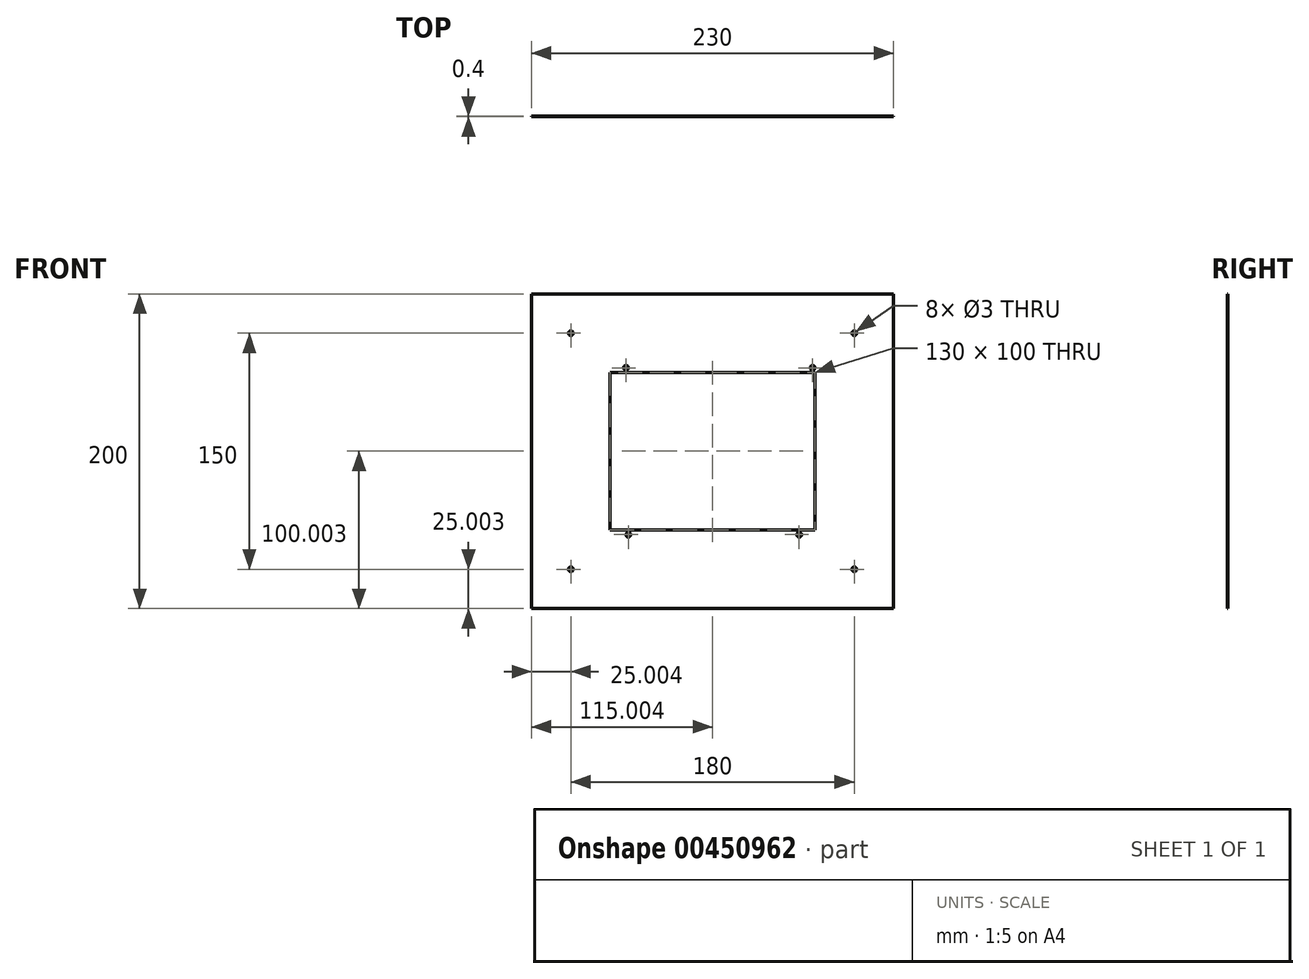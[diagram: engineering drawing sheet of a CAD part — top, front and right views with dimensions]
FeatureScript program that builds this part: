
annotation { "Feature Type Name" : "Feature", "Feature Type Description" : "" }
export const myFeature = defineFeature(function(context is Context, id is Id, definition is map)
    precondition{}
    {
        {
            var Q0;
            Q0=qCreatedBy(makeId("Front.planeOp"),FACE);
            var sketch = newSketch(context, id + "F0", { "sketchPlane" : qUnion([Q0])});
            skLineSegment(sketch, "E0.bottom", {"start": v(-111.43, 122.4) * mm, "end": v(118.57, 122.4) * mm});
            skLineSegment(sketch, "E0.top", {"start": v(-111.43, -77.6) * mm, "end": v(118.57, -77.6) * mm});
            skLineSegment(sketch, "E0.left", {"start": v(-111.43, 122.4) * mm, "end": v(-111.43, -77.6) * mm});
            skLineSegment(sketch, "E0.right", {"start": v(118.57, 122.4) * mm, "end": v(118.57, -77.6) * mm});
            skSolve(sketch);
        }
        {
            var Q0;
            Q0 = qSketchRegion(id + "F0", true);
            extrude(context, id + "F1", {"entities" : qUnion([Q0]), "depth" : 0.4 * mm, "offsetDistance" : 25 * mm});
        }
        {
            var Q0;
            Q0=makeQuery(id+"F1.opExtrude","CAP_FACE",FACE,{"disambiguationData":[OSD([sQuery(id+"F0.wireOp",EDGE,"E0.bottom"),sQuery(id+"F0.wireOp",EDGE,"E0.top"),sQuery(id+"F0.wireOp",EDGE,"E0.left"),sQuery(id+"F0.wireOp",EDGE,"E0.right")])],"isStart":false});
            var sketch = newSketch(context, id + "F2", { "sketchPlane" : qUnion([Q0])});
            skLineSegment(sketch, "E1.bottom", {"start": v(-61.43, -27.6) * mm, "end": v(68.57, -27.6) * mm});
            skLineSegment(sketch, "E1.top", {"start": v(-61.43, 72.4) * mm, "end": v(68.57, 72.4) * mm});
            skLineSegment(sketch, "E1.left", {"start": v(-61.43, -27.6) * mm, "end": v(-61.43, 72.4) * mm});
            skLineSegment(sketch, "E1.right", {"start": v(68.57, -27.6) * mm, "end": v(68.57, 72.4) * mm});
            skCircle(sketch, "E2", {"center": v(-49.93, -30.6) * mm, "radius": 1.5 * mm});
            skCircle(sketch, "E3", {"center": v(58.57, -30.6) * mm, "radius": 1.5 * mm});
            skCircle(sketch, "E4", {"center": v(67.07, 75.4) * mm, "radius": 1.5 * mm});
            skCircle(sketch, "E5", {"center": v(-51.43, 75.4) * mm, "radius": 1.5 * mm});
            skCircle(sketch, "E6", {"center": v(-86.43, -52.6) * mm, "radius": 1.5 * mm});
            skCircle(sketch, "E7", {"center": v(93.57, -52.6) * mm, "radius": 1.5 * mm});
            skCircle(sketch, "E8", {"center": v(-86.43, 97.4) * mm, "radius": 1.5 * mm});
            skCircle(sketch, "E9", {"center": v(93.57, 97.4) * mm, "radius": 1.5 * mm});
            skSolve(sketch);
        }
        {
            var Q0;
            Q0 = qSketchRegion(id + "F2", true);
            extrude(context, id + "F3", {"entities" : qUnion([Q0]), "operationType" : NewBodyOperationType.REMOVE, "oppositeDirection" : true, "depth" : 25 * mm, "offsetDistance" : 25 * mm});
        }
    });
